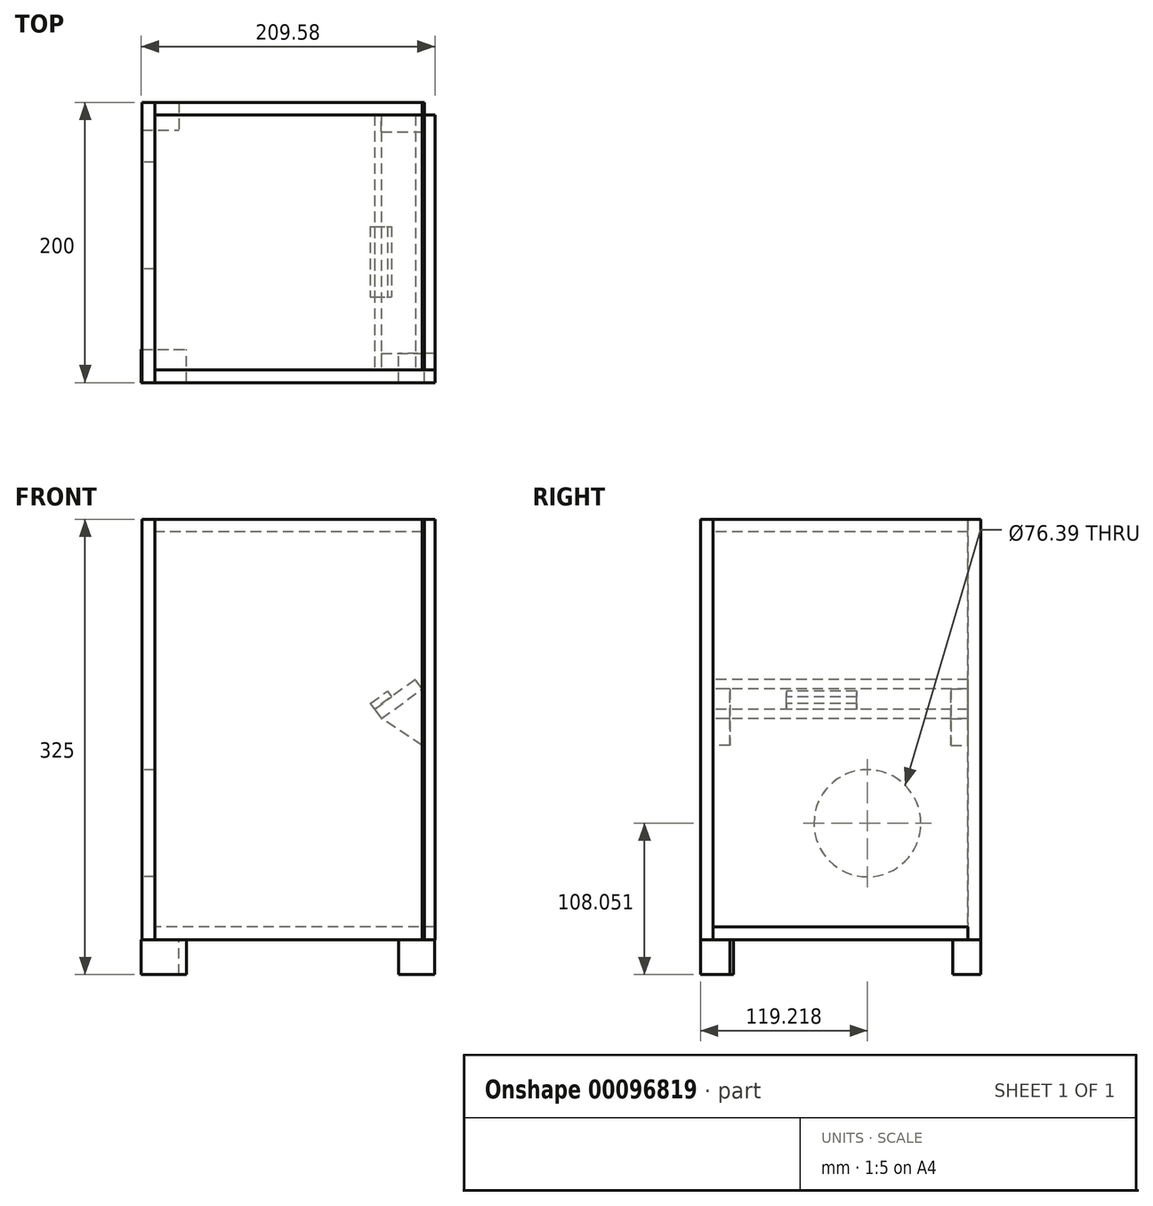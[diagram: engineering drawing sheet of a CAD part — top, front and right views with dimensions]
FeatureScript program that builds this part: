
annotation { "Feature Type Name" : "Feature", "Feature Type Description" : "" }
export const myFeature = defineFeature(function(context is Context, id is Id, definition is map)
    precondition{}
    {
        {
            var Q0;
            Q0=qCreatedBy(makeId("Front.planeOp"),FACE);
            var sketch = newSketch(context, id + "F0", { "sketchPlane" : qUnion([Q0])});
            skLineSegment(sketch, "E0.bottom", {"start": v(0, 0) * mm, "end": v(200, 0) * mm});
            skLineSegment(sketch, "E0.top", {"start": v(0, 300) * mm, "end": v(200, 300) * mm});
            skLineSegment(sketch, "E0.left", {"start": v(0, 0) * mm, "end": v(0, 300) * mm});
            skLineSegment(sketch, "E0.right", {"start": v(200, 0) * mm, "end": v(200, 300) * mm});
            skSolve(sketch);
        }
        {
            var Q0;
            Q0=makeQuery(id+"F0.imprint","IMPRINT",FACE,{"disambiguationData":[TD([[makeQuery(id+"F0.imprint","IMPRINT",EDGE,{"derivedFrom":sQuery(id+"F0.wireOp",EDGE,"E0.bottom")}),1.0]])]});
            var Q1;
            Q1 = qSketchRegion(id + "FuhadVC8PwTdHEQ_0", true);
            var Q2;
            Q2 = qSketchRegion(id + "F2", true);
            extrude(context, id + "F1", {"entities" : qUnion([Q0, Q1, Q2]), "oppositeDirection" : true, "depth" : 9 * mm});
        }
        {
            var Q0;
            Q0=makeQuery(id+"F1.opExtrude","CAP_FACE",FACE,{"disambiguationData":[OSD([sQuery(id+"F0.wireOp",EDGE,"E0.bottom"),sQuery(id+"F0.wireOp",EDGE,"E0.top"),sQuery(id+"F0.wireOp",EDGE,"E0.left"),sQuery(id+"F0.wireOp",EDGE,"E0.right")])],"isStart":false});
            var sketch = newSketch(context, id + "F2", { "sketchPlane" : qUnion([Q0])});
            skLineSegment(sketch, "E1", {"start": v(-191, 178.9) * mm, "end": v(-191, 138.6) * mm});
            skLineSegment(sketch, "E2", {"start": v(-191, 138.6) * mm, "end": v(-161.81, 157.7) * mm});
            skLineSegment(sketch, "E3", {"start": v(-161.81, 157.7) * mm, "end": v(-191, 178.9) * mm});
            skSolve(sketch);
        }
        {
            var Q0;
            Q0 = qSketchRegion(id + "F2", true);
            extrude(context, id + "F3", {"entities" : qUnion([Q0]), "depth" : 12 * mm});
        }
        {
            var Q0;
            Q0=makeQuery(id+"F1.opExtrude","CAP_FACE",FACE,{"disambiguationData":[OSD([sQuery(id+"F0.wireOp",EDGE,"E0.bottom"),sQuery(id+"F0.wireOp",EDGE,"E0.top"),sQuery(id+"F0.wireOp",EDGE,"E0.left"),sQuery(id+"F0.wireOp",EDGE,"E0.right")])],"isStart":false});
            var sketch = newSketch(context, id + "F4", { "sketchPlane" : qUnion([Q0])});
            skLineSegment(sketch, "E4", {"start": v(-161.81, 157.7) * mm, "end": v(-191, 178.9) * mm});
            skLineSegment(sketch, "E5", {"start": v(-191, 178.9) * mm, "end": v(-186.06, 185.7) * mm});
            skLineSegment(sketch, "E6", {"start": v(-186.06, 185.7) * mm, "end": v(-156.88, 164.5) * mm});
            skLineSegment(sketch, "E7", {"start": v(-156.88, 164.5) * mm, "end": v(-161.81, 157.7) * mm});
            skSolve(sketch);
        }
        {
            var Q0;
            Q0=makeQuery(id+"F4.imprint","IMPRINT",FACE,{"disambiguationData":[TD([[makeQuery(id+"F4.imprint","IMPRINT",EDGE,{"derivedFrom":sQuery(id+"F4.wireOp",EDGE,"E4")}),-1.0]])]});
            extrude(context, id + "F5", {"entities" : qUnion([Q0]), "depth" : 182 * mm});
        }
        {
            var Q0;
            Q0=makeQuery(id+"F5.opExtrude","CAP_FACE",FACE,{"disambiguationData":[OSD([sQuery(id+"F4.wireOp",EDGE,"E4"),sQuery(id+"F4.wireOp",EDGE,"E5"),sQuery(id+"F4.wireOp",EDGE,"E6"),sQuery(id+"F4.wireOp",EDGE,"E7")])],"isStart":false});
            var sketch = newSketch(context, id + "F6", { "sketchPlane" : qUnion([Q0])});
            skLineSegment(sketch, "E8", {"start": v(-191, 178.9) * mm, "end": v(-191, 138.6) * mm});
            skLineSegment(sketch, "E9", {"start": v(-191, 138.6) * mm, "end": v(-161.81, 157.7) * mm});
            skLineSegment(sketch, "E10", {"start": v(-161.81, 157.7) * mm, "end": v(-191, 178.9) * mm});
            skSolve(sketch);
        }
        {
            var Q0;
            Q0 = qSketchRegion(id + "F6", true);
            extrude(context, id + "F7", {"entities" : qUnion([Q0]), "oppositeDirection" : true, "depth" : 12 * mm});
        }
        {
            var Q0;
            Q0=makeQuery(id+"F5.opExtrude","SWEPT_FACE",FACE,{"disambiguationData":[OSD([sQuery(id+"F4.wireOp",EDGE,"E6")])]});
            var sketch = newSketch(context, id + "F8", { "sketchPlane" : qUnion([Q0])});
            skLineSegment(sketch, "E11.bottom", {"start": v(223.6, 111.48) * mm, "end": v(238.66, 111.48) * mm});
            skLineSegment(sketch, "E11.top", {"start": v(223.6, 61.33) * mm, "end": v(238.66, 61.33) * mm});
            skLineSegment(sketch, "E11.left", {"start": v(223.6, 111.48) * mm, "end": v(223.6, 61.33) * mm});
            skLineSegment(sketch, "E11.right", {"start": v(238.66, 111.48) * mm, "end": v(238.66, 61.33) * mm});
            skSolve(sketch);
        }
        {
            var Q0;
            Q0 = qSketchRegion(id + "F8", true);
            extrude(context, id + "F9", {"entities" : qUnion([Q0]), "depth" : 5 * mm});
        }
        {
            var Q0;
            Q0=makeQuery(id+"F1.opExtrude","CAP_FACE",FACE,{"disambiguationData":[OSD([sQuery(id+"F0.wireOp",EDGE,"E0.bottom"),sQuery(id+"F0.wireOp",EDGE,"E0.top"),sQuery(id+"F0.wireOp",EDGE,"E0.left"),sQuery(id+"F0.wireOp",EDGE,"E0.right")])],"isStart":false});
            var sketch = newSketch(context, id + "F10", { "sketchPlane" : qUnion([Q0])});
            skLineSegment(sketch, "E12.bottom", {"start": v(-191, 300) * mm, "end": v(0, 300) * mm});
            skLineSegment(sketch, "E12.top", {"start": v(-191, 291) * mm, "end": v(0, 291) * mm});
            skLineSegment(sketch, "E12.left", {"start": v(-191, 300) * mm, "end": v(-191, 291) * mm});
            skLineSegment(sketch, "E12.right", {"start": v(0, 300) * mm, "end": v(0, 291) * mm});
            skSolve(sketch);
        }
        {
            var Q0;
            Q0 = qSketchRegion(id + "F10", true);
            extrude(context, id + "F11", {"entities" : qUnion([Q0]), "depth" : 182 * mm});
        }
        {
            var Q0;
            Q0=makeQuery(id+"F1.opExtrude","CAP_FACE",FACE,{"disambiguationData":[OSD([sQuery(id+"F0.wireOp",EDGE,"E0.bottom"),sQuery(id+"F0.wireOp",EDGE,"E0.top"),sQuery(id+"F0.wireOp",EDGE,"E0.left"),sQuery(id+"F0.wireOp",EDGE,"E0.right")])],"isStart":false});
            var sketch = newSketch(context, id + "F12", { "sketchPlane" : qUnion([Q0])});
            skLineSegment(sketch, "E13.bottom", {"start": v(-200, 9) * mm, "end": v(0, 9) * mm});
            skLineSegment(sketch, "E13.top", {"start": v(-200, 0) * mm, "end": v(0, 0) * mm});
            skLineSegment(sketch, "E13.left", {"start": v(-200, 9) * mm, "end": v(-200, 0) * mm});
            skLineSegment(sketch, "E13.right", {"start": v(0, 9) * mm, "end": v(0, 0) * mm});
            skSolve(sketch);
        }
        {
            var Q0;
            Q0 = qSketchRegion(id + "F12", true);
            extrude(context, id + "F13", {"entities" : qUnion([Q0]), "depth" : 182 * mm});
        }
        {
            var Q0;
            Q0=makeQuery(id+"F11.opExtrude","CAP_FACE",FACE,{"disambiguationData":[OSD([sQuery(id+"F10.wireOp",EDGE,"E12.bottom"),sQuery(id+"F10.wireOp",EDGE,"E12.top"),sQuery(id+"F10.wireOp",EDGE,"E12.left"),sQuery(id+"F10.wireOp",EDGE,"E12.right")])],"isStart":false});
            var sketch = newSketch(context, id + "F14", { "sketchPlane" : qUnion([Q0])});
            skLineSegment(sketch, "E14.bottom", {"start": v(-191, 300) * mm, "end": v(0, 300) * mm});
            skLineSegment(sketch, "E14.top", {"start": v(-191, 0) * mm, "end": v(0, 0) * mm});
            skLineSegment(sketch, "E14.left", {"start": v(-191, 300) * mm, "end": v(-191, 0) * mm});
            skLineSegment(sketch, "E14.right", {"start": v(0, 300) * mm, "end": v(0, 0) * mm});
            skSolve(sketch);
        }
        {
            var Q0;
            Q0=makeQuery(id+"F11.opExtrude","SWEPT_FACE",FACE,{"disambiguationData":[OSD([sQuery(id+"F10.wireOp",EDGE,"E12.left")])]});
            var sketch = newSketch(context, id + "F15", { "sketchPlane" : qUnion([Q0])});
            skLineSegment(sketch, "E15.bottom", {"start": v(0, 299.8) * mm, "end": v(200, 299.8) * mm});
            skLineSegment(sketch, "E15.top", {"start": v(0, 0) * mm, "end": v(200, 0) * mm});
            skLineSegment(sketch, "E15.left", {"start": v(0, 299.8) * mm, "end": v(0, 0) * mm});
            skLineSegment(sketch, "E15.right", {"start": v(200, 299.8) * mm, "end": v(200, 0) * mm});
            skSolve(sketch);
        }
        {
            var Q0;
            Q0 = qSketchRegion(id + "F14", true);
            extrude(context, id + "F16", {"entities" : qUnion([Q0]), "depth" : 9 * mm});
        }
        {
            var Q0;
            Q0=makeQuery(id+"F15.imprint","IMPRINT",FACE,{"disambiguationData":[TD([[makeQuery(id+"F15.imprint","IMPRINT",EDGE,{"derivedFrom":sQuery(id+"F15.wireOp",EDGE,"E15.top")}),1.0]])]});
            var sketch = newSketch(context, id + "F17", { "sketchPlane" : qUnion([Q0])});
            skLineSegment(sketch, "E16.bottom", {"start": v(0, 299.8) * mm, "end": v(200, 299.8) * mm});
            skLineSegment(sketch, "E16.top", {"start": v(0, 0) * mm, "end": v(200, 0) * mm});
            skLineSegment(sketch, "E16.left", {"start": v(0, 299.8) * mm, "end": v(0, 0) * mm});
            skLineSegment(sketch, "E16.right", {"start": v(200, 299.8) * mm, "end": v(200, 0) * mm});
            skSolve(sketch);
        }
        {
            var Q0;
            Q0 = qSketchRegion(id + "F17", true);
            extrude(context, id + "F18", {"entities" : qUnion([Q0]), "depth" : 1.5 * mm});
        }
        {
            var Q0;
            Q0=makeQuery(id+"F16.opExtrude","SWEPT_FACE",FACE,{"disambiguationData":[OSD([sQuery(id+"F14.wireOp",EDGE,"E14.right")])]});
            var sketch = newSketch(context, id + "F19", { "sketchPlane" : qUnion([Q0])});
            skLineSegment(sketch, "E17.bottom", {"start": v(-200, 300) * mm, "end": v(0, 300) * mm});
            skLineSegment(sketch, "E17.top", {"start": v(-200, 0) * mm, "end": v(0, 0) * mm});
            skLineSegment(sketch, "E17.left", {"start": v(-200, 300) * mm, "end": v(-200, 0) * mm});
            skLineSegment(sketch, "E17.right", {"start": v(0, 300) * mm, "end": v(0, 0) * mm});
            skSolve(sketch);
        }
        {
            var Q0;
            Q0 = qSketchRegion(id + "F19", true);
            extrude(context, id + "F20", {"entities" : qUnion([Q0]), "depth" : 9 * mm});
        }
        {
            var Q0;
            Q0=makeQuery(id+"F20.opExtrude","CAP_FACE",FACE,{"disambiguationData":[OSD([sQuery(id+"F19.wireOp",EDGE,"E17.bottom"),sQuery(id+"F19.wireOp",EDGE,"E17.top"),sQuery(id+"F19.wireOp",EDGE,"E17.left"),sQuery(id+"F19.wireOp",EDGE,"E17.right")])],"isStart":false});
            var sketch = newSketch(context, id + "F21", { "sketchPlane" : qUnion([Q0])});
            skCircle(sketch, "E18", {"center": v(-119.22, 83.05) * mm, "radius": 38.2 * mm});
            skSolve(sketch);
        }
        {
            var Q0;
            Q0 = qSketchRegion(id + "F21", true);
            extrude(context, id + "F22", {"entities" : qUnion([Q0]), "operationType" : NewBodyOperationType.REMOVE, "oppositeDirection" : true, "depth" : 30 * mm});
        }
        {
            var Q0;
            Q0=makeQuery(id+"F13.opExtrude","SWEPT_FACE",FACE,{"disambiguationData":[OSD([sQuery(id+"F12.wireOp",EDGE,"E13.top")])]});
            var sketch = newSketch(context, id + "F23", { "sketchPlane" : qUnion([Q0])});
            skLineSegment(sketch, "E19.bottom", {"start": v(-9.58, 0) * mm, "end": v(22.81, 0) * mm});
            skLineSegment(sketch, "E19.top", {"start": v(-9.58, -23.61) * mm, "end": v(22.81, -23.61) * mm});
            skLineSegment(sketch, "E19.left", {"start": v(-9.58, 0) * mm, "end": v(-9.58, -23.61) * mm});
            skLineSegment(sketch, "E19.right", {"start": v(22.81, 0) * mm, "end": v(22.81, -23.61) * mm});
            skSolve(sketch);
        }
        {
            var Q0;
            Q0 = qSketchRegion(id + "F23", true);
            extrude(context, id + "F24", {"entities" : qUnion([Q0]), "depth" : 25 * mm});
        }
        {
            var Q0;
            Q0=makeQuery(id+"F13.opExtrude","SWEPT_FACE",FACE,{"disambiguationData":[OSD([sQuery(id+"F12.wireOp",EDGE,"E13.top")])]});
            var sketch = newSketch(context, id + "F25", { "sketchPlane" : qUnion([Q0])});
            skLineSegment(sketch, "E20.bottom", {"start": v(199.68, 0) * mm, "end": v(174.08, 0) * mm});
            skLineSegment(sketch, "E20.top", {"start": v(199.68, -20.9) * mm, "end": v(174.08, -20.9) * mm});
            skLineSegment(sketch, "E20.left", {"start": v(199.68, 0) * mm, "end": v(199.68, -20.9) * mm});
            skLineSegment(sketch, "E20.right", {"start": v(174.08, 0) * mm, "end": v(174.08, -20.9) * mm});
            skSolve(sketch);
        }
        {
            var Q0;
            Q0 = qSketchRegion(id + "F25", true);
            extrude(context, id + "F26", {"entities" : qUnion([Q0]), "depth" : 25 * mm});
        }
        {
            var Q0;
            Q0=makeQuery(id+"F13.opExtrude","SWEPT_FACE",FACE,{"disambiguationData":[OSD([sQuery(id+"F12.wireOp",EDGE,"E13.top")])]});
            var sketch = newSketch(context, id + "F27", { "sketchPlane" : qUnion([Q0])});
            skLineSegment(sketch, "E21.bottom", {"start": v(-9, -200) * mm, "end": v(17.4, -200) * mm});
            skLineSegment(sketch, "E21.top", {"start": v(-9, -180.08) * mm, "end": v(17.4, -180.08) * mm});
            skLineSegment(sketch, "E21.left", {"start": v(-9, -200) * mm, "end": v(-9, -180.08) * mm});
            skLineSegment(sketch, "E21.right", {"start": v(17.4, -200) * mm, "end": v(17.4, -180.08) * mm});
            skSolve(sketch);
        }
        {
            var Q0;
            Q0 = qSketchRegion(id + "F27", true);
            extrude(context, id + "F28", {"entities" : qUnion([Q0]), "depth" : 25 * mm});
        }
    });
